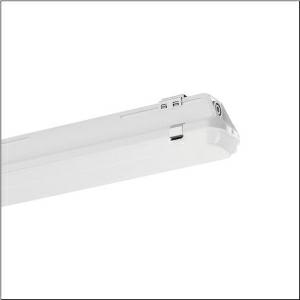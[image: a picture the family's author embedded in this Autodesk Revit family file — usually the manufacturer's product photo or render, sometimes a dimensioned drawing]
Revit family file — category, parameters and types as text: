
# Revit family: monsun_r__21_51fb207l420k_f7be
name_source: partatom
category: Lighting Fixtures
units: mm (PartAtom-declared; Revit-internal decimal feet)

## family parameters
Cut with Voids When Loaded = No
Host = Face
Light Source = No
Part Type = Normal
Room Calculation Point = No
Round Connector Dimension = Use Diameter
Shared = No

## types (1)
- Monsun® 21 (1 x LED, 2620 lm, 17.1 W, 4000K)
    Apparent Load = 17 VA
    CIE Flux Codes = 45 75 93 94 100
    Color Rendering = 80
    Color Temperature = 4000K
    Default Elevation = 1800 mm
    Description = Monsun® 21, damp-proof luminaire, chain hanger, primary optical cover: enclosure, of PC, light emission: direct distribution, primary light characteristic: symmetric, installation type: suspended mounting, surface-mounted, horizontal mounting, vertical mounting, LED, rated luminous flux: 2.620lm, luminous efficacy: 153lm/W, light colour: 840, colour temperature: 4000K, control gear: ON/OFF, with terminal, 3-pole, max. 2.5mm², mains connection: 220..240V, AC, 50/60Hz, rated input power: 17W, housing, of glass-fibre reinforced plastic, uncoated, bright grey, incl. chain hanger, length: 1.299mm, width: 90mm, height: 88mm, clip for enclosure, of stainless steel (V2A), ceiling mounting element, of stainless steel (V2A), chain hanger, of stainless steel (V2A), protection rating (complete): IP66, insulation class (complete): insulation class I (protective earthing), certification: CE, ENEC, VDE, UKCA, protection symbol: D, impact resistance: IK08, permissible operating ambient temperature: -25..+35°C, standard: EN 50419, EN 60598-2-1, corresponds to IFS (International Featured Standards) requirements for safety and quality in the food industry, for indoor or canopied outdoor use, no direct snow, no direct sun, no direct rain, LABS conformity tested according to VDMA 24364:2018-05, contact your sales advisor before using the luminaires in applications with unclear chemical exposure, large temperature fluctuations or condensation-forming humidity, packaging unit: 1 piece
    Height = 88 mm
    Lamp = 1 x LED
    Lamp Light Flux = 2620 lm
    Lamp Power = 17.1 W
    Lamp count = 1
    Length = 1299 mm
    Luminous efficacy = 153 lm/W
    Manufacturer = Siteco
    ModVariant = No
    Model = 51FB207L420K
    Mounting Place = Ceiling
    Mounting Type = Surface mounted
    Number of Poles = 1
    OnlyDefault = Yes
    Power Factor = 1
    Product Name = Monsun® 21
    Product group = damp-proof luminaire
    ProductGroupID = 300
    Protection Class = Protection class I
    Protection Degree = IP 66
    RLX_Detail_Level = 1
    RLX_Emergency_Light_Flux = 0 lm
    RLX_Emergency_Type = 0
    RLX_Emergency_Type_DB = No
    RlxData = <blob elided: 89613 chars, md5=a52ecb14>
    Socket = socket
    Standby Power = 0 W
    System Light Flux = 2620 lm
    System Power = 17 W
    Type Comments = Product without accessories
    Type Image = l_1319656.jpg
    URL = http://relux.com
    VarID = ---
    Voltage = 0 V
    Weight = 0.00 kg
    Width = 90 mm

## geometry (parser evidence)
native form markers: Blend x4, Sweep x12
no freeform markers — native parametric forms only
